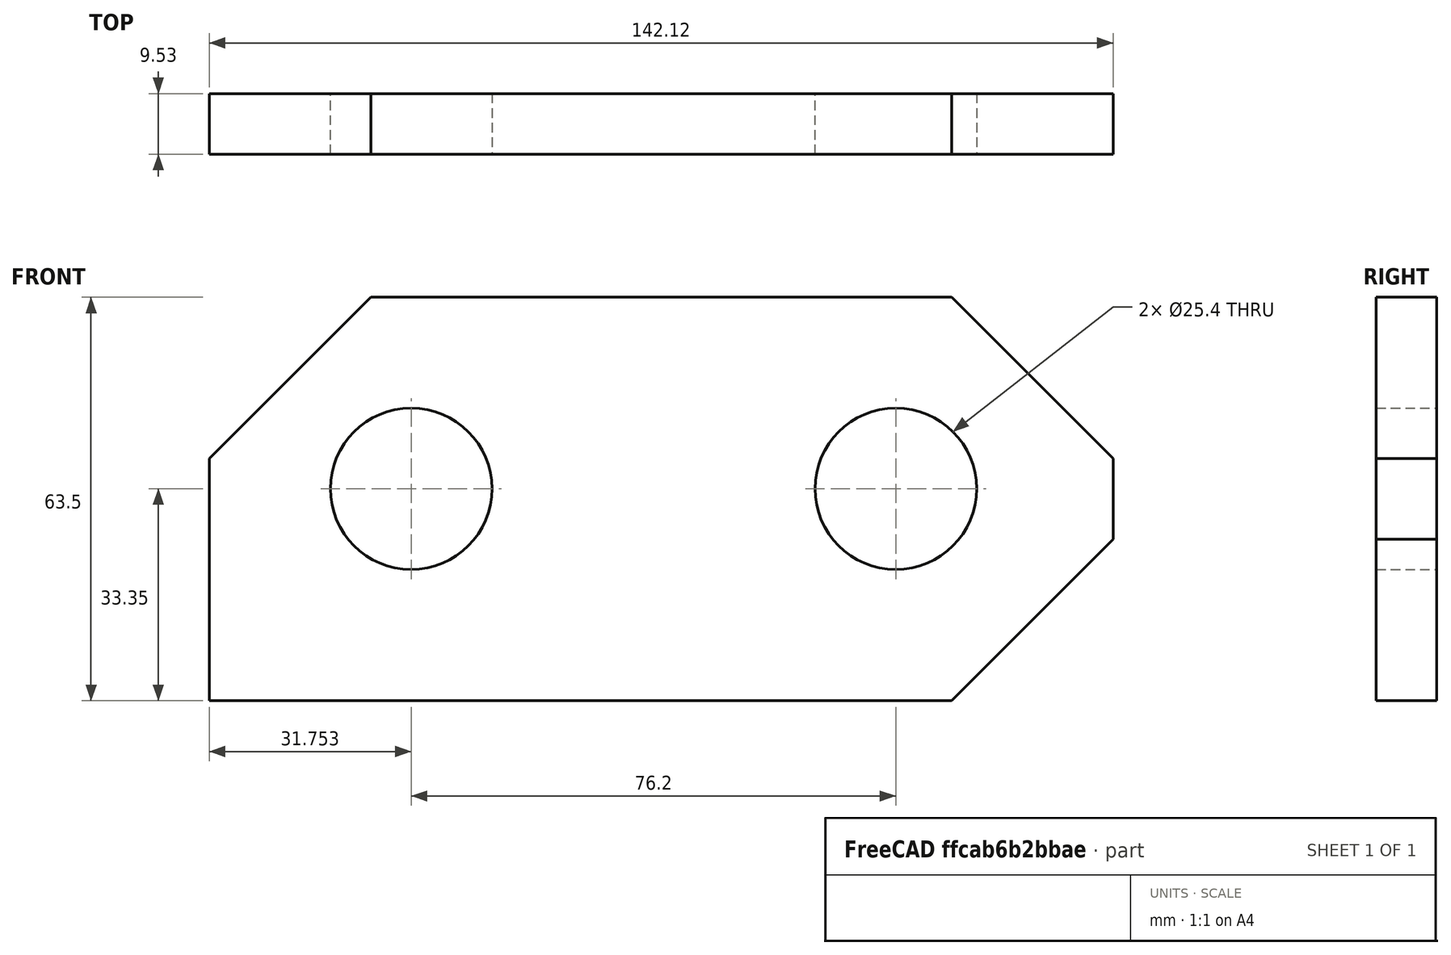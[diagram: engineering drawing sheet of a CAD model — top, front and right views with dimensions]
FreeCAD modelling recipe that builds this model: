
FCSTD DOCUMENT  (FreeCAD 0.16R6702 (Git))
Label: TrackChainLink
License: All rights reserved
LicenseURL: http://en.wikipedia.org/wiki/All_rights_reserved
objects: Sketcher::SketchObject×1, PartDesign::Pad×1
note: 3 computed .brp shape members not serialized (recipe doc carries the construction recipe); baked Part::Feature solids carry a one-line shape summary decoded from their .brp

FEATURE [Sketcher::SketchObject] Sketch
  Placement = pos=(0,0,0) rot=(-1,0,0;4.71239rad)
  sketch-geometry (9):
    g0: LineSegment StartX=-60.1573 StartY=57.66 StartZ=0 EndX=31.1554 EndY=57.66 EndZ=0
    g1: LineSegment StartX=56.5554 StartY=32.26 StartZ=0 EndX=56.5554 EndY=19.56 EndZ=0
    g2: LineSegment StartX=31.1554 StartY=-5.83998 StartZ=0 EndX=-85.5573 EndY=-5.83998 EndZ=0
    g3: LineSegment StartX=-85.5573 StartY=-5.83998 StartZ=0 EndX=-85.5573 EndY=32.26 EndZ=0
    g4: Circle CenterX=-53.8073 CenterY=27.5102 CenterZ=0 NormalX=0 NormalY=0 NormalZ=1 Radius=12.7
    g5: Circle CenterX=22.3927 CenterY=27.5102 CenterZ=0 NormalX=0 NormalY=0 NormalZ=1 Radius=12.7
    g6: LineSegment StartX=-60.1573 StartY=57.66 StartZ=0 EndX=-85.5573 EndY=32.26 EndZ=0
    g7: LineSegment StartX=31.1554 StartY=57.66 StartZ=0 EndX=56.5554 EndY=32.26 EndZ=0
    g8: LineSegment StartX=56.5554 StartY=19.56 StartZ=0 EndX=31.1554 EndY=-5.83998 EndZ=0
  constraints (25):
    c: Coincident(g2,g3)
    c: Horizontal(g2)
    c: Vertical(g1)
    c: Vertical(g3)
    c: Radius(g4) = 12.7
    c: DistanceX(g2,g4) = 31.75
    c: DistanceY(g2,g4) = 33.3502
    c: Equal(g4,g5) = 12.7
    c: DistanceX(g4,g5) = 76.2
    c: DistanceY(g2,g5) = 33.3502
    c: Coincident(g3,g6)
    c: PointOnObject(g0,g6)
    c: Coincident(g6,g0)
    c: DistanceX(g2,g0) = 25.4
    c: Coincident(g0,g7)
    c: Coincident(g1,g7)
    c: DistanceX(g0,g1) = 25.4
    c: DistanceY(g2,g0) = 63.5
    c: DistanceY(g2,g0) = 63.5
    c: DistanceY(g2,g1) = 38.1
    c: DistanceY(g3,g0) = 25.4
    c: Coincident(g1,g8)
    c: Coincident(g2,g8)
    c: DistanceY(g2,g1) = 25.4
    c: DistanceX(g2,g1) = 25.4
FEATURE [PartDesign::Pad] Pad
  Length = 9.525
  Length2 = 100
  Placement = pos=(0,0,0) rot=(-1,0,0;4.71239rad)
  Sketch = -> Sketch
  Type = 0
